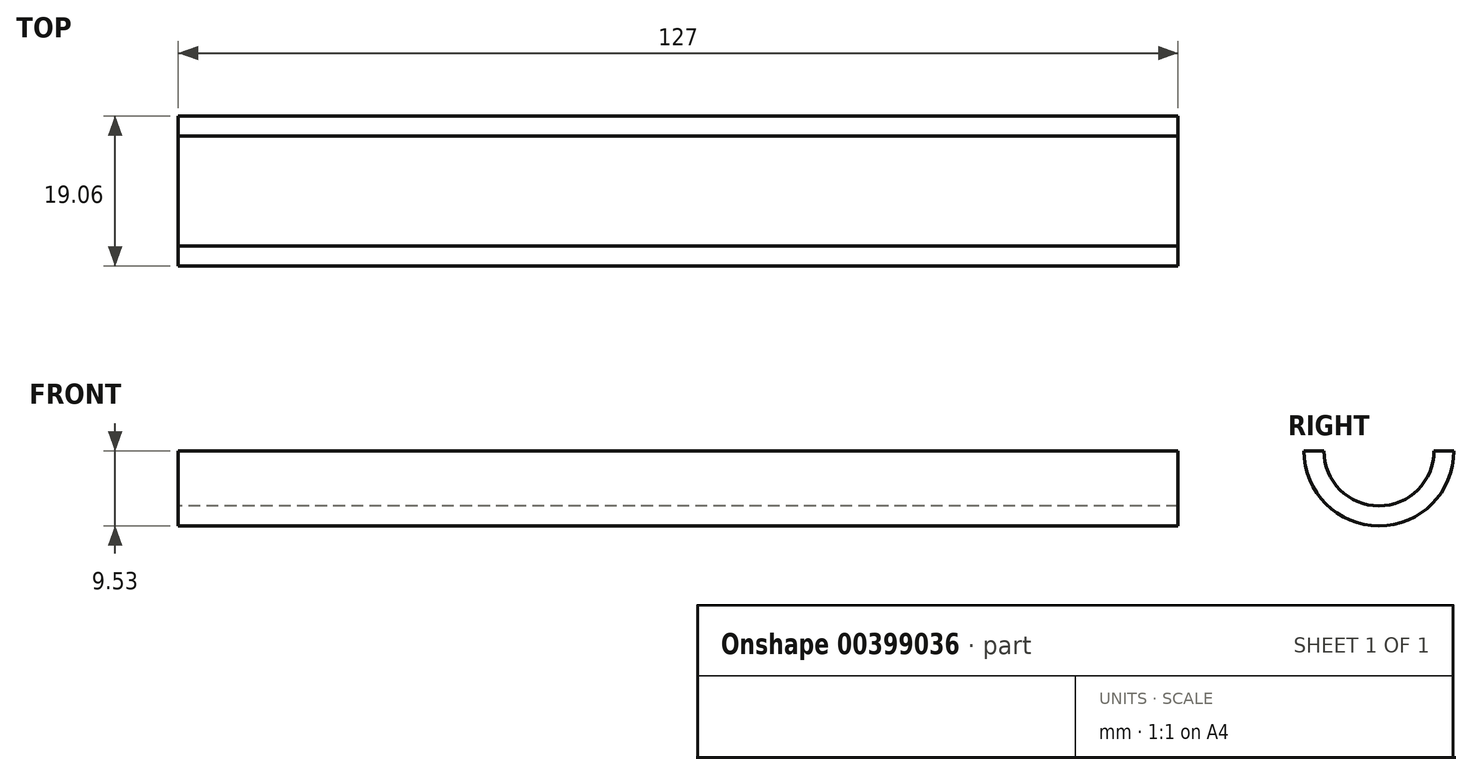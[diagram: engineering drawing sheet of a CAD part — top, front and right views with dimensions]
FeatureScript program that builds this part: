
annotation { "Feature Type Name" : "Feature", "Feature Type Description" : "" }
export const myFeature = defineFeature(function(context is Context, id is Id, definition is map)
    precondition{}
    {
        {
            var Q0;
            Q0=qCreatedBy(makeId("Right.planeOp"),FACE);
            var sketch = newSketch(context, id + "F0", { "sketchPlane" : qUnion([Q0])});
            skArc(sketch, "E0", {"start": v(-9.53, 0) * mm, "mid": v(0, -9.53) * mm, "end": v(9.53, 0) * mm});
            skLineSegment(sketch, "E1", {"start": v(-9.53, 0) * mm, "end": v(9.53, 0) * mm});
            skSolve(sketch);
        }
        {
            var Q0;
            Q0=qSketchRegion(id+"F0",true);
            extrude(context, id + "F1", {"entities" : qUnion([Q0]), "depth" : 127 * mm, "symmetric" : true});
        }
        {
            var Q0;
            Q0=makeQuery(id+"F1.opExtrude","CAP_FACE",FACE,{"disambiguationData":[OSD([sQuery(id+"F0.wireOp",EDGE,"E0"),sQuery(id+"F0.wireOp",EDGE,"E1")])],"isStart":false});
            var Q1;
            Q1=makeQuery(id+"F1.opExtrude","SWEPT_FACE",FACE,{"disambiguationData":[OSD([sQuery(id+"F0.wireOp",EDGE,"E1")])]});
            var Q2;
            Q2=makeQuery(id+"F1.opExtrude","CAP_FACE",FACE,{"disambiguationData":[OSD([sQuery(id+"F0.wireOp",EDGE,"E0"),sQuery(id+"F0.wireOp",EDGE,"E1")])],"isStart":true});
            shell(context, id + "F2", {"entities" : qUnion([Q0, Q1, Q2]), "thickness" : 2.54 * mm});
        }
    });
